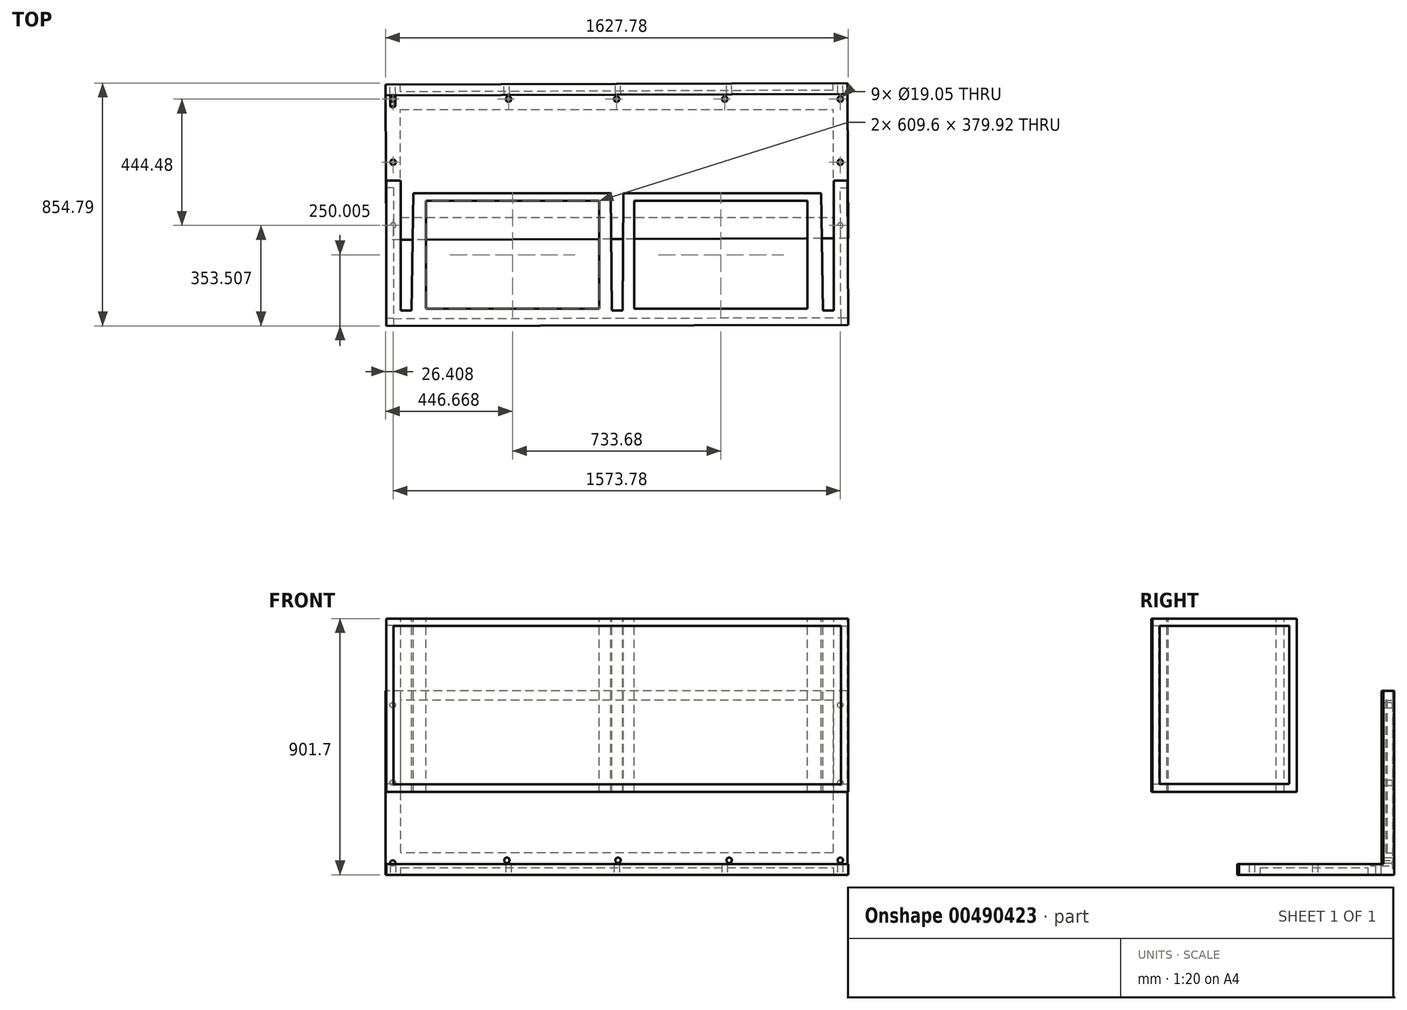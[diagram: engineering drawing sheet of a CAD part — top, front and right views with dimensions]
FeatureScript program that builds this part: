
annotation { "Feature Type Name" : "Feature", "Feature Type Description" : "" }
export const myFeature = defineFeature(function(context is Context, id is Id, definition is map)
    precondition{}
    {
        {
            var Q0;
            Q0=qCreatedBy(makeId("Top.planeOp"),FACE);
            var sketch = newSketch(context, id + "F0", { "sketchPlane" : qUnion([Q0])});
            skLineSegment(sketch, "E0", {"start": v(-1490.15, -82.87) * mm, "end": v(-1490.15, -540.07) * mm});
            skLineSegment(sketch, "E1", {"start": v(-1490.15, -540.07) * mm, "end": v(-1452.05, -540.07) * mm});
            skLineSegment(sketch, "E2", {"start": v(-1490.15, -82.87) * mm, "end": v(33.85, -82.87) * mm});
            skLineSegment(sketch, "E3", {"start": v(33.85, -82.87) * mm, "end": v(33.85, -540.07) * mm});
            skLineSegment(sketch, "E4", {"start": v(33.85, -540.07) * mm, "end": v(-4.25, -540.07) * mm});
            skLineSegment(sketch, "E5", {"start": v(-1445.7, -127.32) * mm, "end": v(-1452.05, -540.07) * mm});
            skLineSegment(sketch, "E6", {"start": v(-10.6, -127.32) * mm, "end": v(-4.25, -540.07) * mm});
            skLineSegment(sketch, "E7", {"start": v(-1445.7, -127.32) * mm, "end": v(-750.38, -127.32) * mm});
            skLineSegment(sketch, "E8", {"start": v(-10.6, -127.32) * mm, "end": v(-705.93, -127.32) * mm});
            skLineSegment(sketch, "E9", {"start": v(-705.93, -127.32) * mm, "end": v(-709.1, -540.07) * mm});
            skLineSegment(sketch, "E10", {"start": v(-750.38, -127.32) * mm, "end": v(-747.2, -540.07) * mm});
            skLineSegment(sketch, "E11", {"start": v(-709.1, -540.07) * mm, "end": v(-747.2, -540.07) * mm});
            skLineSegment(sketch, "E12", {"start": v(33.85, -540.07) * mm, "end": v(33.85, -590.87) * mm});
            skLineSegment(sketch, "E13", {"start": v(82.6, -32.07) * mm, "end": v(84.65, -590.87) * mm});
            skLineSegment(sketch, "E14", {"start": v(-1540.94, -35.7) * mm, "end": v(-1540.94, -594.5) * mm});
            skLineSegment(sketch, "E15", {"start": v(-1540.94, -35.7) * mm, "end": v(82.6, -32.07) * mm});
            skLineSegment(sketch, "E16", {"start": v(-1540.94, -594.5) * mm, "end": v(84.65, -590.87) * mm});
            skSolve(sketch);
        }
        {
            var Q0;
            Q0=makeQuery(id+"F0.imprint","IMPRINT",FACE,{"disambiguationData":[TD([[makeQuery(id+"F0.imprint","IMPRINT",EDGE,{"derivedFrom":sQuery(id+"F0.wireOp",EDGE,"E0")}),-1.0]])]});
            extrude(context, id + "F1", {"entities" : qUnion([Q0]), "depth" : -609.6 * mm});
        }
        {
            var Q0;
            Q0=makeQuery(id+"F1.opExtrude","CAP_FACE",FACE,{"disambiguationData":[OSD([sQuery(id+"F0.wireOp",EDGE,"E0"),sQuery(id+"F0.wireOp",EDGE,"E1"),sQuery(id+"F0.wireOp",EDGE,"E2"),sQuery(id+"F0.wireOp",EDGE,"E3"),sQuery(id+"F0.wireOp",EDGE,"E4"),sQuery(id+"F0.wireOp",EDGE,"E5"),sQuery(id+"F0.wireOp",EDGE,"E6"),sQuery(id+"F0.wireOp",EDGE,"E7"),sQuery(id+"F0.wireOp",EDGE,"E8"),sQuery(id+"F0.wireOp",EDGE,"E9"),sQuery(id+"F0.wireOp",EDGE,"E10"),sQuery(id+"F0.wireOp",EDGE,"E11"),sQuery(id+"F0.wireOp",EDGE,"E13"),sQuery(id+"F0.wireOp",EDGE,"E14"),sQuery(id+"F0.wireOp",EDGE,"E15"),sQuery(id+"F0.wireOp",EDGE,"E16")])],"isStart":true});
            var sketch = newSketch(context, id + "F2", { "sketchPlane" : qUnion([Q0])});
            skLineSegment(sketch, "E17.bottom", {"start": v(-653.62, -154.54) * mm, "end": v(-44.02, -154.54) * mm});
            skLineSegment(sketch, "E17.top", {"start": v(-653.62, -539.96) * mm, "end": v(-44.02, -539.96) * mm});
            skLineSegment(sketch, "E17.left", {"start": v(-653.62, -154.54) * mm, "end": v(-653.62, -539.96) * mm});
            skLineSegment(sketch, "E17.right", {"start": v(-44.02, -154.54) * mm, "end": v(-44.02, -539.96) * mm});
            skLineSegment(sketch, "E18.bottom", {"start": v(-791.66, -154.54) * mm, "end": v(-1401.26, -154.54) * mm});
            skLineSegment(sketch, "E18.top", {"start": v(-791.66, -534.45) * mm, "end": v(-1401.26, -534.45) * mm});
            skLineSegment(sketch, "E18.left", {"start": v(-791.66, -154.54) * mm, "end": v(-791.66, -534.45) * mm});
            skLineSegment(sketch, "E18.right", {"start": v(-1401.26, -154.54) * mm, "end": v(-1401.26, -534.45) * mm});
            skSolve(sketch);
        }
        {
            var Q0;
            Q0=makeQuery(id+"F2.imprint","IMPRINT",FACE,{"disambiguationData":[TD([[makeQuery(id+"F2.imprint","IMPRINT",EDGE,{"derivedFrom":sQuery(id+"F2.wireOp",EDGE,"E18.bottom")}),1.0]])]});
            extrude(context, id + "F3", {"entities" : qUnion([Q0]), "operationType" : NewBodyOperationType.REMOVE, "oppositeDirection" : true, "depth" : 609.6 * mm});
        }
        {
            var Q0;
            Q0=makeQuery(id+"F1.opExtrude","CAP_FACE",FACE,{"disambiguationData":[OSD([sQuery(id+"F0.wireOp",EDGE,"E0"),sQuery(id+"F0.wireOp",EDGE,"E1"),sQuery(id+"F0.wireOp",EDGE,"E2"),sQuery(id+"F0.wireOp",EDGE,"E3"),sQuery(id+"F0.wireOp",EDGE,"E4"),sQuery(id+"F0.wireOp",EDGE,"E5"),sQuery(id+"F0.wireOp",EDGE,"E6"),sQuery(id+"F0.wireOp",EDGE,"E7"),sQuery(id+"F0.wireOp",EDGE,"E8"),sQuery(id+"F0.wireOp",EDGE,"E9"),sQuery(id+"F0.wireOp",EDGE,"E10"),sQuery(id+"F0.wireOp",EDGE,"E11"),sQuery(id+"F0.wireOp",EDGE,"E13"),sQuery(id+"F0.wireOp",EDGE,"E14"),sQuery(id+"F0.wireOp",EDGE,"E15"),sQuery(id+"F0.wireOp",EDGE,"E16")])],"isStart":true});
            var sketch = newSketch(context, id + "F4", { "sketchPlane" : qUnion([Q0])});
            skLineSegment(sketch, "E19.bottom", {"start": v(-667.58, -154.54) * mm, "end": v(-57.98, -154.54) * mm});
            skLineSegment(sketch, "E19.top", {"start": v(-667.58, -534.45) * mm, "end": v(-57.98, -534.45) * mm});
            skLineSegment(sketch, "E19.left", {"start": v(-667.58, -154.54) * mm, "end": v(-667.58, -534.45) * mm});
            skLineSegment(sketch, "E19.right", {"start": v(-57.98, -154.54) * mm, "end": v(-57.98, -534.45) * mm});
            skSolve(sketch);
        }
        {
            var Q0;
            Q0=makeQuery(id+"F4.imprint","IMPRINT",FACE,{"disambiguationData":[TD([[makeQuery(id+"F4.imprint","IMPRINT",EDGE,{"derivedFrom":sQuery(id+"F4.wireOp",EDGE,"E19.bottom")}),-1.0]])]});
            extrude(context, id + "F5", {"entities" : qUnion([Q0]), "operationType" : NewBodyOperationType.REMOVE, "oppositeDirection" : true, "depth" : 609.6 * mm});
        }
        {
            var Q0;
            Q0=makeQuery(id+"F1.opExtrude","CAP_FACE",FACE,{"disambiguationData":[OSD([sQuery(id+"F0.wireOp",EDGE,"E0"),sQuery(id+"F0.wireOp",EDGE,"E1"),sQuery(id+"F0.wireOp",EDGE,"E2"),sQuery(id+"F0.wireOp",EDGE,"E3"),sQuery(id+"F0.wireOp",EDGE,"E4"),sQuery(id+"F0.wireOp",EDGE,"E5"),sQuery(id+"F0.wireOp",EDGE,"E6"),sQuery(id+"F0.wireOp",EDGE,"E7"),sQuery(id+"F0.wireOp",EDGE,"E8"),sQuery(id+"F0.wireOp",EDGE,"E9"),sQuery(id+"F0.wireOp",EDGE,"E10"),sQuery(id+"F0.wireOp",EDGE,"E11"),sQuery(id+"F0.wireOp",EDGE,"E13"),sQuery(id+"F0.wireOp",EDGE,"E14"),sQuery(id+"F0.wireOp",EDGE,"E15"),sQuery(id+"F0.wireOp",EDGE,"E16")])],"isStart":true});
            var sketch = newSketch(context, id + "F6", { "sketchPlane" : qUnion([Q0])});
            skLineSegment(sketch, "E20", {"start": v(-1540.94, -82.87) * mm, "end": v(82.78, -82.87) * mm});
            skLineSegment(sketch, "E21", {"start": v(82.78, -82.87) * mm, "end": v(82.6, -32.07) * mm});
            skLineSegment(sketch, "E22", {"start": v(-1540.94, -35.7) * mm, "end": v(82.6, -32.07) * mm});
            skLineSegment(sketch, "E23", {"start": v(-1540.94, -35.7) * mm, "end": v(-1540.94, -82.87) * mm});
            skSolve(sketch);
        }
        {
            var Q0;
            Q0=qSketchRegion(id+"F6",true);
            extrude(context, id + "F7", {"entities" : qUnion([Q0]), "operationType" : NewBodyOperationType.REMOVE, "oppositeDirection" : true, "depth" : 609.6 * mm});
        }
        {
            var Q0;
            Q0=makeQuery(id+"F1.opExtrude","SWEPT_FACE",FACE,{"disambiguationData":[OSD([sQuery(id+"F0.wireOp",EDGE,"E13")])]});
            var sketch = newSketch(context, id + "F8", { "sketchPlane" : qUnion([Q0])});
            skLineSegment(sketch, "E24.bottom", {"start": v(-38.1, 0) * mm, "end": v(0, 0) * mm});
            skLineSegment(sketch, "E24.top", {"start": v(-38.1, -609.6) * mm, "end": v(0, -609.6) * mm});
            skLineSegment(sketch, "E24.left", {"start": v(-38.1, 0) * mm, "end": v(-38.1, -609.6) * mm});
            skLineSegment(sketch, "E24.right", {"start": v(0, 0) * mm, "end": v(0, -609.6) * mm});
            skLineSegment(sketch, "E25.bottom", {"start": v(0, -609.6) * mm, "end": v(-546.1, -609.6) * mm});
            skLineSegment(sketch, "E25.top", {"start": v(0, -647.7) * mm, "end": v(-546.1, -647.7) * mm});
            skLineSegment(sketch, "E25.left", {"start": v(0, -609.6) * mm, "end": v(0, -647.7) * mm});
            skLineSegment(sketch, "E25.right", {"start": v(-546.1, -609.6) * mm, "end": v(-546.1, -647.7) * mm});
            skSolve(sketch);
        }
        {
            var Q0;
            Q0=makeQuery(id+"F8.imprint","IMPRINT",FACE,{"disambiguationData":[TD([[makeQuery(id+"F8.imprint","IMPRINT",EDGE,{"derivedFrom":sQuery(id+"F8.wireOp",EDGE,"E24.bottom")}),-1.0]])]});
            var Q1;
            Q1=makeQuery(id+"F8.imprint","IMPRINT",FACE,{"disambiguationData":[TD([[makeQuery(id+"F8.imprint","IMPRINT",EDGE,{"derivedFrom":sQuery(id+"F8.wireOp",EDGE,"E25.top")}),-1.0]])]});
            extrude(context, id + "F9", {"entities" : qUnion([Q0, Q1]), "operationType" : NewBodyOperationType.ADD, "depth" : 1625.6 * mm});
        }
        {
            var Q0;
            Q0=makeQuery(id+"F9.opExtrude","SWEPT_BODY",BODY,{"disambiguationData":[OSD([sQuery(id+"F8.wireOp",EDGE,"E24.bottom"),sQuery(id+"F8.wireOp",EDGE,"E24.left"),sQuery(id+"F8.wireOp",EDGE,"E24.right"),sQuery(id+"F8.wireOp",EDGE,"E25.bottom"),sQuery(id+"F8.wireOp",EDGE,"E25.top"),sQuery(id+"F8.wireOp",EDGE,"E25.left"),sQuery(id+"F8.wireOp",EDGE,"E25.right")])]});
            transform(context, id + "F10", {"entities" : qUnion([Q0]), "transformType" : TransformType.TRANSLATION_3D, "dx" : -1625.6 * mm, "dy" : 254 * mm, "dz" : -254 * mm, "makeCopy" : false});
        }
        {
            var Q0;
            Q0=makeQuery(id+"F1.opExtrude","SWEPT_FACE",FACE,{"disambiguationData":[OSD([sQuery(id+"F0.wireOp",EDGE,"E16")])]});
            var sketch = newSketch(context, id + "F11", { "sketchPlane" : qUnion([Q0])});
            skLineSegment(sketch, "E26", {"start": v(-1465.88, 0) * mm, "end": v(-1465.88, -25.4) * mm});
            skLineSegment(sketch, "E27", {"start": v(-1465.88, -609.6) * mm, "end": v(-1465.88, -584.2) * mm});
            skLineSegment(sketch, "E28", {"start": v(83.33, -561.8) * mm, "end": v(57.93, -561.8) * mm});
            skLineSegment(sketch, "E29", {"start": v(-1542.27, -290.2) * mm, "end": v(-1516.87, -290.2) * mm});
            skLineSegment(sketch, "E30.bottom", {"start": v(-1516.87, -25.4) * mm, "end": v(57.75, -25.4) * mm});
            skLineSegment(sketch, "E30.top", {"start": v(-1516.87, -583.33) * mm, "end": v(57.75, -583.33) * mm});
            skLineSegment(sketch, "E30.left", {"start": v(-1516.87, -25.4) * mm, "end": v(-1516.87, -583.33) * mm});
            skLineSegment(sketch, "E30.right", {"start": v(57.75, -25.4) * mm, "end": v(57.75, -583.33) * mm});
            skSolve(sketch);
        }
        {
            var Q0;
            Q0=qSketchRegion(id+"F11",true);
            extrude(context, id + "F12", {"entities" : qUnion([Q0]), "operationType" : NewBodyOperationType.REMOVE, "oppositeDirection" : true, "depth" : 25.4 * mm});
        }
        {
            var Q0;
            Q0=makeQuery(id+"F1.opExtrude","SWEPT_FACE",FACE,{"disambiguationData":[OSD([sQuery(id+"F0.wireOp",EDGE,"E13")])]});
            var sketch = newSketch(context, id + "F13", { "sketchPlane" : qUnion([Q0])});
            skLineSegment(sketch, "E31", {"start": v(-591.17, -58.34) * mm, "end": v(-565.77, -58.34) * mm});
            skLineSegment(sketch, "E32", {"start": v(-337.17, 0) * mm, "end": v(-337.17, -25.4) * mm});
            skLineSegment(sketch, "E33", {"start": v(-83.17, -304.8) * mm, "end": v(-108.57, -304.8) * mm});
            skLineSegment(sketch, "E34", {"start": v(-337.17, -609.6) * mm, "end": v(-337.17, -584.2) * mm});
            skLineSegment(sketch, "E35.bottom", {"start": v(-565.77, -25.4) * mm, "end": v(-109.45, -25.4) * mm});
            skLineSegment(sketch, "E35.top", {"start": v(-565.77, -581.67) * mm, "end": v(-109.45, -581.67) * mm});
            skLineSegment(sketch, "E35.left", {"start": v(-565.77, -25.4) * mm, "end": v(-565.77, -581.67) * mm});
            skLineSegment(sketch, "E35.right", {"start": v(-109.45, -25.4) * mm, "end": v(-109.45, -581.67) * mm});
            skSolve(sketch);
        }
        {
            var Q0;
            Q0=qSketchRegion(id+"F13",true);
            extrude(context, id + "F14", {"entities" : qUnion([Q0]), "operationType" : NewBodyOperationType.REMOVE, "oppositeDirection" : true, "depth" : 25.4 * mm});
        }
        {
            var Q0;
            Q0=makeQuery(id+"F1.opExtrude","SWEPT_FACE",FACE,{"disambiguationData":[OSD([sQuery(id+"F0.wireOp",EDGE,"E14")])]});
            var sketch = newSketch(context, id + "F15", { "sketchPlane" : qUnion([Q0])});
            skLineSegment(sketch, "E36", {"start": v(82.87, -290.2) * mm, "end": v(108.27, -290.2) * mm});
            skLineSegment(sketch, "E37", {"start": v(338.69, 0) * mm, "end": v(338.69, -25.22) * mm});
            skLineSegment(sketch, "E38", {"start": v(594.5, -276.95) * mm, "end": v(569.1, -276.95) * mm});
            skLineSegment(sketch, "E39", {"start": v(338.69, -609.6) * mm, "end": v(338.69, -584.2) * mm});
            skLineSegment(sketch, "E40.bottom", {"start": v(108.27, -25.22) * mm, "end": v(567.89, -25.22) * mm});
            skLineSegment(sketch, "E40.top", {"start": v(108.27, -581.67) * mm, "end": v(567.89, -581.67) * mm});
            skLineSegment(sketch, "E40.left", {"start": v(108.27, -25.22) * mm, "end": v(108.27, -581.67) * mm});
            skLineSegment(sketch, "E40.right", {"start": v(567.89, -25.22) * mm, "end": v(567.89, -581.67) * mm});
            skSolve(sketch);
        }
        {
            var Q0;
            Q0=qSketchRegion(id+"F15",true);
            extrude(context, id + "F16", {"entities" : qUnion([Q0]), "operationType" : NewBodyOperationType.REMOVE, "oppositeDirection" : true, "depth" : 25.4 * mm});
        }
        {
            var Q0;
            Q0=makeQuery(id+"F9.opExtrude","SWEPT_FACE",FACE,{"disambiguationData":[OSD([sQuery(id+"F8.wireOp",EDGE,"E24.right"),sQuery(id+"F8.wireOp",EDGE,"E25.left")])]});
            var sketch = newSketch(context, id + "F17", { "sketchPlane" : qUnion([Q0])});
            skPoint(sketch, "E41", {"position": v(-58.02, -304.8) * mm});
            skPoint(sketch, "E42", {"position": v(-58.02, -577.85) * mm});
            skPoint(sketch, "E43", {"position": v(-58.02, -850.9) * mm});
            skSolve(sketch);
        }
        {
            var Q0;
            Q0=sQuery(id+"F17.wireOp",VERTEX,"E41");
            var Q1;
            Q1=sQuery(id+"F17.wireOp",VERTEX,"E42");
            var Q2;
            Q2=sQuery(id+"F17.wireOp",VERTEX,"E43");
            var Q3;
            Q3=makeQuery(id+"F9.opExtrude","SWEPT_BODY",BODY,{"disambiguationData":[OSD([sQuery(id+"F8.wireOp",EDGE,"E24.bottom"),sQuery(id+"F8.wireOp",EDGE,"E24.left"),sQuery(id+"F8.wireOp",EDGE,"E24.right"),sQuery(id+"F8.wireOp",EDGE,"E25.bottom"),sQuery(id+"F8.wireOp",EDGE,"E25.top"),sQuery(id+"F8.wireOp",EDGE,"E25.left"),sQuery(id+"F8.wireOp",EDGE,"E25.right")])]});
            hole(context, id + "F18", {"style" : HoleStyle.SIMPLE, "endStyle" : HoleEndStyle.BLIND, "holeDiameter" : 19.05 * mm, "holeDepth" : 76.2 * mm, "isTappedThrough" : true, "tappedDepth" : 12.7 * mm, "tapClearance" : 3, "locations" : qUnion([Q0, Q1, Q2]), "scope" : qUnion([Q3])});
        }
        {
            var Q0;
            Q0=makeQuery(id+"F9.opExtrude","SWEPT_FACE",FACE,{"disambiguationData":[OSD([sQuery(id+"F8.wireOp",EDGE,"E24.right"),sQuery(id+"F8.wireOp",EDGE,"E25.left")])]});
            var sketch = newSketch(context, id + "F19", { "sketchPlane" : qUnion([Q0])});
            skPoint(sketch, "E44", {"position": v(333.14, -850.9) * mm});
            skPoint(sketch, "E45", {"position": v(724.3, -850.9) * mm});
            skPoint(sketch, "E46", {"position": v(1115.46, -850.9) * mm});
            skPoint(sketch, "E47", {"position": v(1516.78, -860.42) * mm});
            skPoint(sketch, "E48", {"position": v(1516.78, -577.85) * mm});
            skPoint(sketch, "E49", {"position": v(1516.78, -304.8) * mm});
            skSolve(sketch);
        }
        {
            var Q0;
            Q0=sQuery(id+"F19.wireOp",VERTEX,"E44");
            var Q1;
            Q1=sQuery(id+"F19.wireOp",VERTEX,"E45");
            var Q2;
            Q2=sQuery(id+"F19.wireOp",VERTEX,"E46");
            var Q3;
            Q3=sQuery(id+"F19.wireOp",VERTEX,"E47");
            var Q4;
            Q4=sQuery(id+"F19.wireOp",VERTEX,"E48");
            var Q5;
            Q5=sQuery(id+"F19.wireOp",VERTEX,"E49");
            var Q6;
            Q6=makeQuery(id+"F9.opExtrude","SWEPT_BODY",BODY,{"disambiguationData":[OSD([sQuery(id+"F8.wireOp",EDGE,"E24.bottom"),sQuery(id+"F8.wireOp",EDGE,"E24.left"),sQuery(id+"F8.wireOp",EDGE,"E24.right"),sQuery(id+"F8.wireOp",EDGE,"E25.bottom"),sQuery(id+"F8.wireOp",EDGE,"E25.top"),sQuery(id+"F8.wireOp",EDGE,"E25.left"),sQuery(id+"F8.wireOp",EDGE,"E25.right")])]});
            hole(context, id + "F20", {"style" : HoleStyle.SIMPLE, "endStyle" : HoleEndStyle.BLIND, "holeDiameter" : 19.05 * mm, "holeDepth" : 76.2 * mm, "isTappedThrough" : true, "tappedDepth" : 12.7 * mm, "tapClearance" : 3, "locations" : qUnion([Q0, Q1, Q2, Q3, Q4, Q5]), "scope" : qUnion([Q6])});
        }
        {
            var Q0;
            Q0=makeQuery(id+"F9.opExtrude","SWEPT_FACE",FACE,{"disambiguationData":[OSD([sQuery(id+"F8.wireOp",EDGE,"E24.right"),sQuery(id+"F8.wireOp",EDGE,"E25.left")])]});
            var sketch = newSketch(context, id + "F21", { "sketchPlane" : qUnion([Q0])});
            skLineSegment(sketch, "E50", {"start": v(-83.42, -374.66) * mm, "end": v(-32.62, -374.66) * mm});
            skLineSegment(sketch, "E51", {"start": v(0, -901.7) * mm, "end": v(0, -825.5) * mm});
            skLineSegment(sketch, "E52", {"start": v(1542.18, -649.58) * mm, "end": v(1491.38, -649.58) * mm});
            skLineSegment(sketch, "E53.bottom", {"start": v(-32.62, -286.88) * mm, "end": v(1490.1, -286.88) * mm});
            skLineSegment(sketch, "E53.top", {"start": v(-32.62, -825.12) * mm, "end": v(1490.1, -825.12) * mm});
            skLineSegment(sketch, "E53.left", {"start": v(-32.62, -286.88) * mm, "end": v(-32.62, -825.12) * mm});
            skLineSegment(sketch, "E53.right", {"start": v(1490.1, -286.88) * mm, "end": v(1490.1, -825.12) * mm});
            skSolve(sketch);
        }
        {
            var Q0;
            {var subQ3=sQuery(id+"F21.wireOp",EDGE,"E53.bottom");Q0=makeQuery(id+"F21.imprint","IMPRINT",FACE,{"disambiguationData":[TD([[makeQuery(id+"F21.imprint","IMPRINT",EDGE,{"derivedFrom":subQ3}),-1.0]])]});}
            extrude(context, id + "F22", {"entities" : qUnion([Q0]), "operationType" : NewBodyOperationType.REMOVE, "oppositeDirection" : true, "depth" : 25.4 * mm});
        }
        {
            var Q0;
            Q0=makeQuery(id+"F9.opExtrude","SWEPT_FACE",FACE,{"disambiguationData":[OSD([sQuery(id+"F8.wireOp",EDGE,"E25.top")])]});
            var sketch = newSketch(context, id + "F23", { "sketchPlane" : qUnion([Q0])});
            skLineSegment(sketch, "E54", {"start": v(-1491.32, 18.75) * mm, "end": v(-1516.72, 18.75) * mm});
            skLineSegment(sketch, "E55", {"start": v(-1491.32, 241) * mm, "end": v(-1516.72, 241) * mm});
            skLineSegment(sketch, "E56", {"start": v(-1491.32, -203.49) * mm, "end": v(-1516.72, -203.49) * mm});
            skLineSegment(sketch, "E57", {"start": v(31.66, 241) * mm, "end": v(57.06, 241) * mm});
            skLineSegment(sketch, "E58", {"start": v(31.66, 18.75) * mm, "end": v(57.06, 18.75) * mm});
            skLineSegment(sketch, "E59", {"start": v(31.66, -203.49) * mm, "end": v(57.06, -203.49) * mm});
            skPoint(sketch, "E60", {"position": v(-1516.72, 241) * mm});
            skPoint(sketch, "E61", {"position": v(-1516.72, 18.75) * mm});
            skPoint(sketch, "E62", {"position": v(-1516.72, -203.49) * mm});
            skLineSegment(sketch, "E63", {"start": v(-1491.32, -203.49) * mm, "end": v(-1491.32, -228.89) * mm});
            skLineSegment(sketch, "E64", {"start": v(-1491.32, -228.89) * mm, "end": v(-1110.32, -228.89) * mm});
            skLineSegment(sketch, "E65", {"start": v(31.66, -203.49) * mm, "end": v(31.66, -228.89) * mm});
            skLineSegment(sketch, "E66", {"start": v(31.66, -228.89) * mm, "end": v(-349.34, -228.89) * mm});
            skLineSegment(sketch, "E67", {"start": v(-1110.32, -228.89) * mm, "end": v(-729.83, -228.89) * mm});
            skPoint(sketch, "E68", {"position": v(-1110.32, -228.89) * mm});
            skPoint(sketch, "E69", {"position": v(-729.83, -228.89) * mm});
            skPoint(sketch, "E70", {"position": v(-349.34, -228.89) * mm});
            skPoint(sketch, "E71", {"position": v(31.66, -228.89) * mm});
            skPoint(sketch, "E72", {"position": v(-1491.32, -228.89) * mm});
            skPoint(sketch, "E73", {"position": v(57.06, -203.49) * mm});
            skPoint(sketch, "E74", {"position": v(57.06, 18.75) * mm});
            skPoint(sketch, "E75", {"position": v(57.06, 241) * mm});
            skPoint(sketch, "E76", {"position": v(-1110.32, -203.49) * mm});
            skPoint(sketch, "E77", {"position": v(-729.83, -203.49) * mm});
            skPoint(sketch, "E78", {"position": v(-349.34, -203.49) * mm});
            skSolve(sketch);
        }
        {
            var Q0;
            Q0=sQuery(id+"F23.wireOp",VERTEX,"E60");
            var Q1;
            Q1=sQuery(id+"F23.wireOp",VERTEX,"E61");
            var Q2;
            Q2=sQuery(id+"F23.wireOp",VERTEX,"E62");
            var Q3;
            Q3=sQuery(id+"F23.wireOp",VERTEX,"E76");
            var Q4;
            Q4=sQuery(id+"F23.wireOp",VERTEX,"E78");
            var Q5;
            Q5=sQuery(id+"F23.wireOp",VERTEX,"E77");
            var Q6;
            Q6=sQuery(id+"F23.wireOp",VERTEX,"E73");
            var Q7;
            Q7=sQuery(id+"F23.wireOp",VERTEX,"E74");
            var Q8;
            Q8=sQuery(id+"F23.wireOp",VERTEX,"E75");
            var Q9;
            Q9=makeQuery(id+"F9.opExtrude","SWEPT_BODY",BODY,{"disambiguationData":[OSD([sQuery(id+"F8.wireOp",EDGE,"E24.bottom"),sQuery(id+"F8.wireOp",EDGE,"E24.left"),sQuery(id+"F8.wireOp",EDGE,"E24.right"),sQuery(id+"F8.wireOp",EDGE,"E25.bottom"),sQuery(id+"F8.wireOp",EDGE,"E25.top"),sQuery(id+"F8.wireOp",EDGE,"E25.left"),sQuery(id+"F8.wireOp",EDGE,"E25.right")])]});
            hole(context, id + "F24", {"style" : HoleStyle.SIMPLE, "endStyle" : HoleEndStyle.BLIND, "holeDiameter" : 19.05 * mm, "holeDepth" : 76.2 * mm, "isTappedThrough" : true, "tappedDepth" : 12.7 * mm, "tapClearance" : 3, "locations" : qUnion([Q0, Q1, Q2, Q3, Q4, Q5, Q6, Q7, Q8]), "scope" : qUnion([Q9])});
        }
        {
            var Q0;
            Q0=makeQuery(id+"F9.opExtrude","SWEPT_FACE",FACE,{"disambiguationData":[OSD([sQuery(id+"F8.wireOp",EDGE,"E25.top")])]});
            var sketch = newSketch(context, id + "F25", { "sketchPlane" : qUnion([Q0])});
            skLineSegment(sketch, "E79", {"start": v(-1541.71, 129.47) * mm, "end": v(-1490.91, 129.28) * mm});
            skLineSegment(sketch, "E80", {"start": v(83.71, 78.8) * mm, "end": v(32.91, 78.98) * mm});
            skLineSegment(sketch, "E81", {"start": v(-728.32, 288.8) * mm, "end": v(-728.32, 212.6) * mm});
            skLineSegment(sketch, "E82.bottom", {"start": v(-1490.91, 212.6) * mm, "end": v(32.91, 212.6) * mm});
            skLineSegment(sketch, "E82.top", {"start": v(-1490.91, -167.3) * mm, "end": v(32.91, -167.3) * mm});
            skLineSegment(sketch, "E82.left", {"start": v(-1490.91, 212.6) * mm, "end": v(-1490.91, -167.3) * mm});
            skLineSegment(sketch, "E82.right", {"start": v(32.91, 212.6) * mm, "end": v(32.91, -167.3) * mm});
            skSolve(sketch);
        }
        {
            var Q0;
            {var subQ4=sQuery(id+"F25.wireOp",EDGE,"E82.top");Q0=makeQuery(id+"F25.imprint","IMPRINT",FACE,{"disambiguationData":[TD([[makeQuery(id+"F25.imprint","IMPRINT",EDGE,{"derivedFrom":subQ4}),1.0]])]});}
            extrude(context, id + "F26", {"entities" : qUnion([Q0]), "operationType" : NewBodyOperationType.REMOVE, "oppositeDirection" : true, "depth" : 25.4 * mm});
        }
    });
